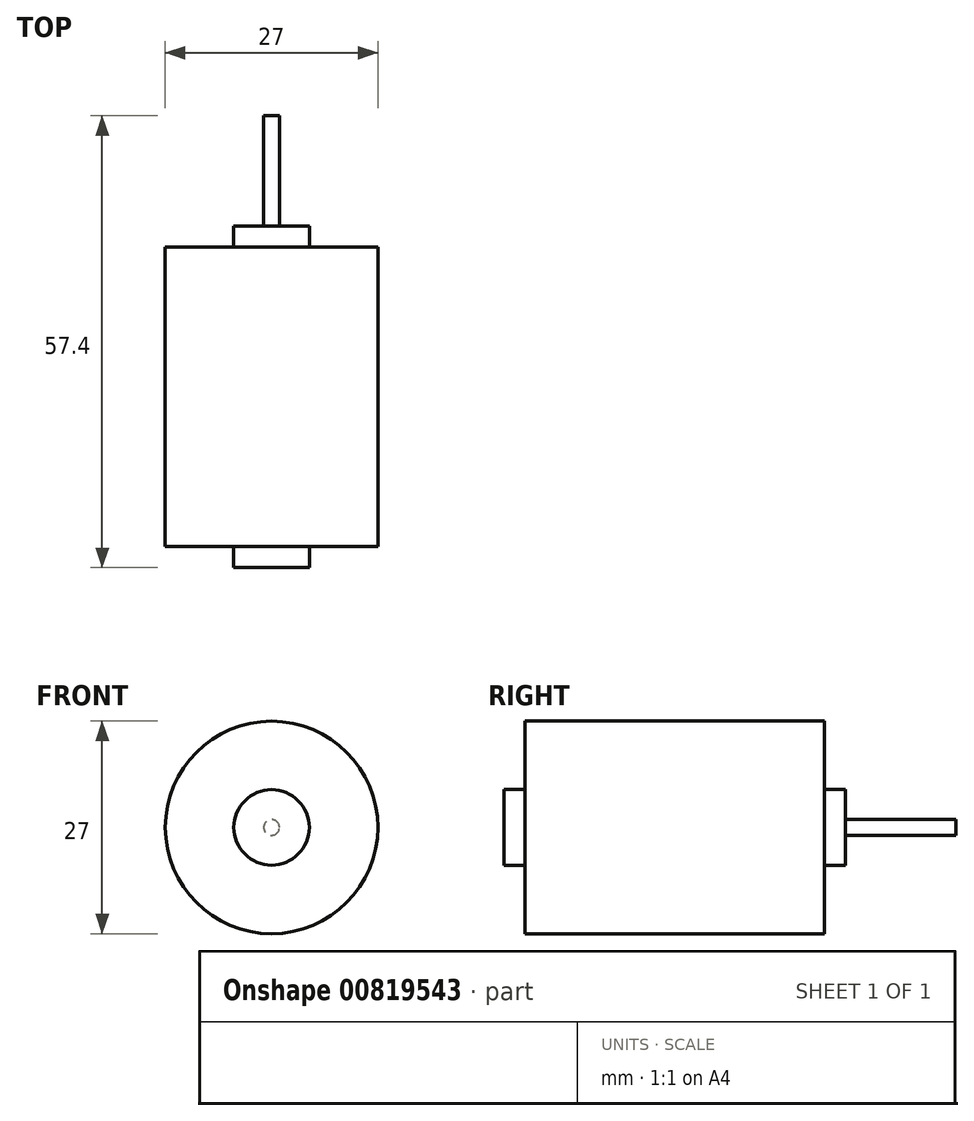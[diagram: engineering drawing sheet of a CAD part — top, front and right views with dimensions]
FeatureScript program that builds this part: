
annotation { "Feature Type Name" : "Feature", "Feature Type Description" : "" }
export const myFeature = defineFeature(function(context is Context, id is Id, definition is map)
    precondition{}
    {
        {
            var Q0;
            Q0=qCreatedBy(makeId("Top.planeOp"),FACE);
            var sketch = newSketch(context, id + "F0", { "sketchPlane" : qUnion([Q0])});
            skLineSegment(sketch, "E0", {"start": v(0, 0) * mm, "end": v(4.8, 0) * mm});
            skLineSegment(sketch, "E1", {"start": v(4.8, 0) * mm, "end": v(4.8, 2.7) * mm});
            skLineSegment(sketch, "E2", {"start": v(4.8, 2.7) * mm, "end": v(13.5, 2.7) * mm});
            skLineSegment(sketch, "E3", {"start": v(13.5, 2.7) * mm, "end": v(13.5, 40.7) * mm});
            skLineSegment(sketch, "E4", {"start": v(13.5, 40.7) * mm, "end": v(4.8, 40.7) * mm});
            skLineSegment(sketch, "E5", {"start": v(4.8, 40.7) * mm, "end": v(4.8, 43.4) * mm});
            skLineSegment(sketch, "E6", {"start": v(4.8, 43.4) * mm, "end": v(1, 43.4) * mm});
            skLineSegment(sketch, "E7", {"start": v(1, 43.4) * mm, "end": v(1, 57.4) * mm});
            skLineSegment(sketch, "E8", {"start": v(1, 57.4) * mm, "end": v(0, 57.4) * mm});
            skLineSegment(sketch, "E9", {"start": v(0, 57.4) * mm, "end": v(0, 0) * mm});
            skSolve(sketch);
        }
        {
            var Q0;
            Q0=makeQuery(id+"F0.imprint","IMPRINT",FACE,{"disambiguationData":[TD([[makeQuery(id+"F0.imprint","IMPRINT",EDGE,{"derivedFrom":sQuery(id+"F0.wireOp",EDGE,"E0")}),1.0]])]});
            var Q1;
            Q1=sQuery(id+"F0.wireOp",EDGE,"E9");
            revolve(context, id + "F1", {"surfaceOperationType" : NewSurfaceOperationType.NEW, "entities" : qUnion([Q0]), "axis" : qUnion([Q1]), "revolveType" : RevolveType.FULL});
        }
    });
